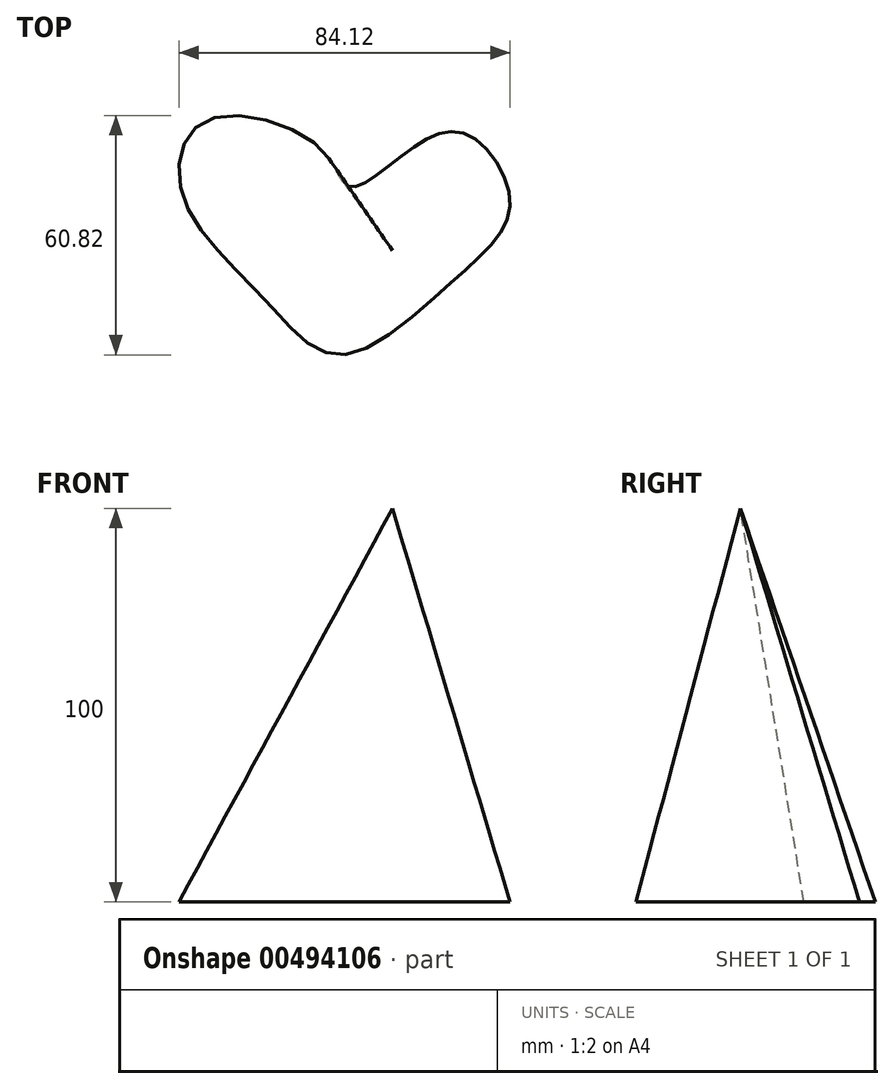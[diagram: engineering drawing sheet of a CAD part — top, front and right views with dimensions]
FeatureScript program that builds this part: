
annotation { "Feature Type Name" : "Feature", "Feature Type Description" : "" }
export const myFeature = defineFeature(function(context is Context, id is Id, definition is map)
    precondition{}
    {
        {
            var Q0;
            Q0=qCreatedBy(makeId("Top.planeOp"),FACE);
            var sketch = newSketch(context, id + "F0", { "sketchPlane" : qUnion([Q0])});
            skFitSpline(sketch, "E0", {"points": [v(-18.36, 25.96) * mm, v(-47.62, 32.85) * mm, v(-53.36, 14.2) * mm, v(-33.57, -11.33) * mm, v(-13.48, -26.54) * mm, v(15.5, -7.6) * mm, v(29.84, 12.2) * mm, v(18.36, 29.7) * mm, v(2.58, 24.24) * mm, v(-10.9, 16.2) * mm, v(-18.36, 25.96) * mm]});
            skPoint(sketch, "E1", {"position": v(0, 0) * mm});
            skPoint(sketch, "E2", {"position": v(-93.52, 71.58) * mm});
            skPoint(sketch, "E3", {"position": v(-5.74, 0) * mm});
            skSolve(sketch);
        }
        {
            var Q0;
            Q0=qCreatedBy(makeId("Top.planeOp"),FACE);
            cPlane(context, id + "F1", {"entities" : qUnion([Q0]), "cplaneType" : CPlaneType.OFFSET, "offset" : 100 * mm, "width" : 150 * mm, "height" : 150 * mm});
        }
        {
            var Q0;
            Q0=qCreatedBy(id+"F1.planeOp",FACE);
            var sketch = newSketch(context, id + "F2", { "sketchPlane" : qUnion([Q0])});
            skPoint(sketch, "E4", {"position": v(0, 0) * mm});
            skSolve(sketch);
        }
        {
            var Q0;
            Q0=sQuery(id+"F2.wireOp",VERTEX,"E4");
            var Q1;
            Q1=makeQuery(id+"F0.imprint","IMPRINT",FACE,{"disambiguationData":[TD([[makeQuery(id+"F0.imprint","IMPRINT",EDGE,{"derivedFrom":sQuery(id+"F0.wireOp",EDGE,"E0")}),1.0]])]});
            loft(context, id + "F3", {"sheetProfilesArray" : [{ "sheetProfileEntities" : qUnion([Q0]) }, { "sheetProfileEntities" : qUnion([Q1]) }]});
        }
    });
